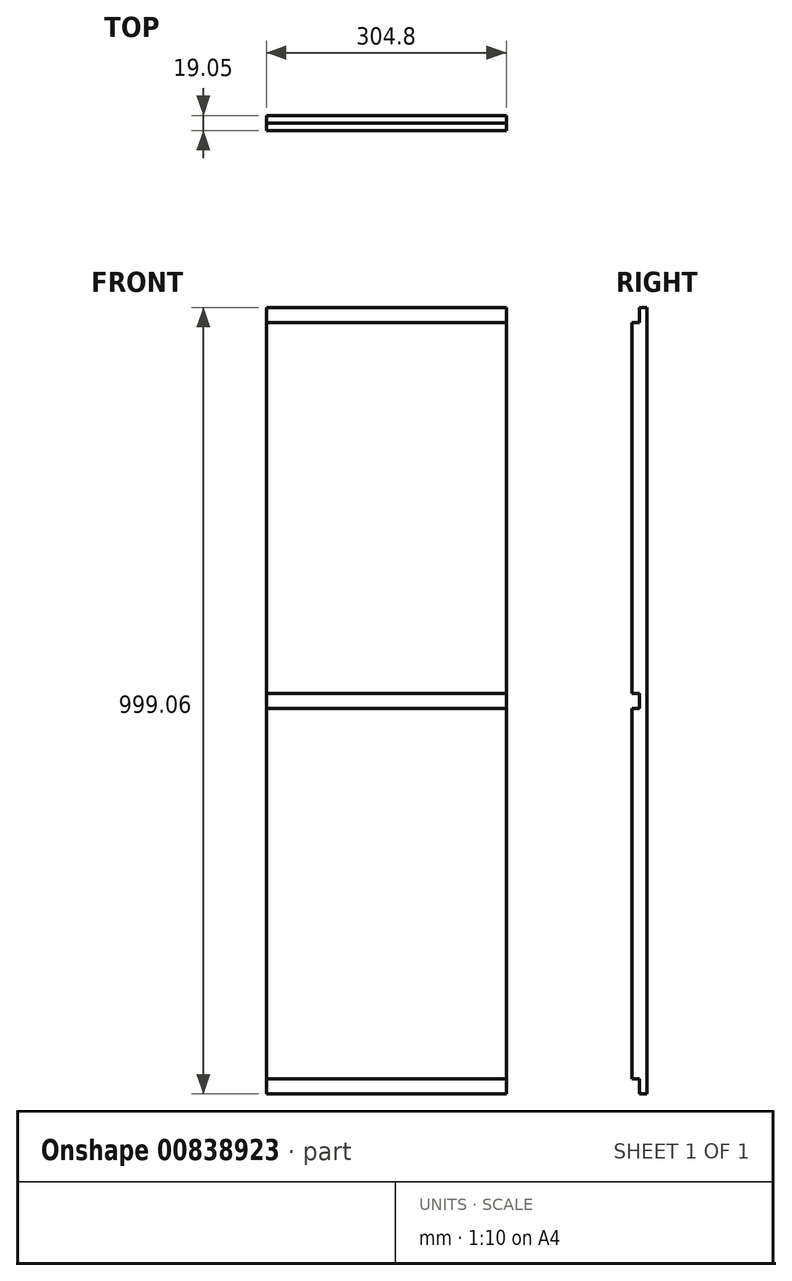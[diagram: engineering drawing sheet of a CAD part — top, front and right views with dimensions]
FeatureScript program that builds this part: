
annotation { "Feature Type Name" : "Feature", "Feature Type Description" : "" }
export const myFeature = defineFeature(function(context is Context, id is Id, definition is map)
    precondition{}
    {
        {
            var Q0;
            Q0=qCreatedBy(makeId("Right.planeOp"),FACE);
            var sketch = newSketch(context, id + "F0", { "sketchPlane" : qUnion([Q0])});
            skLineSegment(sketch, "E0", {"start": v(0, 870.41) * mm, "end": v(0, -128.65) * mm});
            skLineSegment(sketch, "E1", {"start": v(0, -128.65) * mm, "end": v(-9.52, -128.65) * mm});
            skLineSegment(sketch, "E2", {"start": v(-9.52, -128.65) * mm, "end": v(-9.52, -109.6) * mm});
            skLineSegment(sketch, "E3", {"start": v(-9.52, -109.6) * mm, "end": v(-19.05, -109.6) * mm});
            skLineSegment(sketch, "E4", {"start": v(-19.05, 851.36) * mm, "end": v(-9.52, 851.36) * mm});
            skLineSegment(sketch, "E5", {"start": v(-9.52, 851.36) * mm, "end": v(-9.52, 870.41) * mm});
            skLineSegment(sketch, "E6", {"start": v(-9.52, 870.41) * mm, "end": v(0, 870.41) * mm});
            skLineSegment(sketch, "E7", {"start": v(-19.05, 380.4) * mm, "end": v(-9.52, 380.4) * mm});
            skLineSegment(sketch, "E8", {"start": v(-9.52, 380.4) * mm, "end": v(-9.52, 361.36) * mm});
            skLineSegment(sketch, "E9", {"start": v(-9.52, 361.36) * mm, "end": v(-19.05, 361.36) * mm});
            skLineSegment(sketch, "E10.trimOffspring", {"start": v(-19.05, 380.4) * mm, "end": v(-19.05, 851.36) * mm});
            skLineSegment(sketch, "E11", {"start": v(-19.05, 361.36) * mm, "end": v(-19.05, -109.6) * mm});
            skLineSegment(sketch, "E12", {"start": v(-9.52, 870.41) * mm, "end": v(-84.6, 870.41) * mm});
            skSolve(sketch);
        }
        {
            var Q0;
            Q0 = qSketchRegion(id + "F0", true);
            extrude(context, id + "F1", {"entities" : qUnion([Q0]), "depth" : 304.8 * mm, "offsetDistance" : 25.4 * mm});
        }
    });
